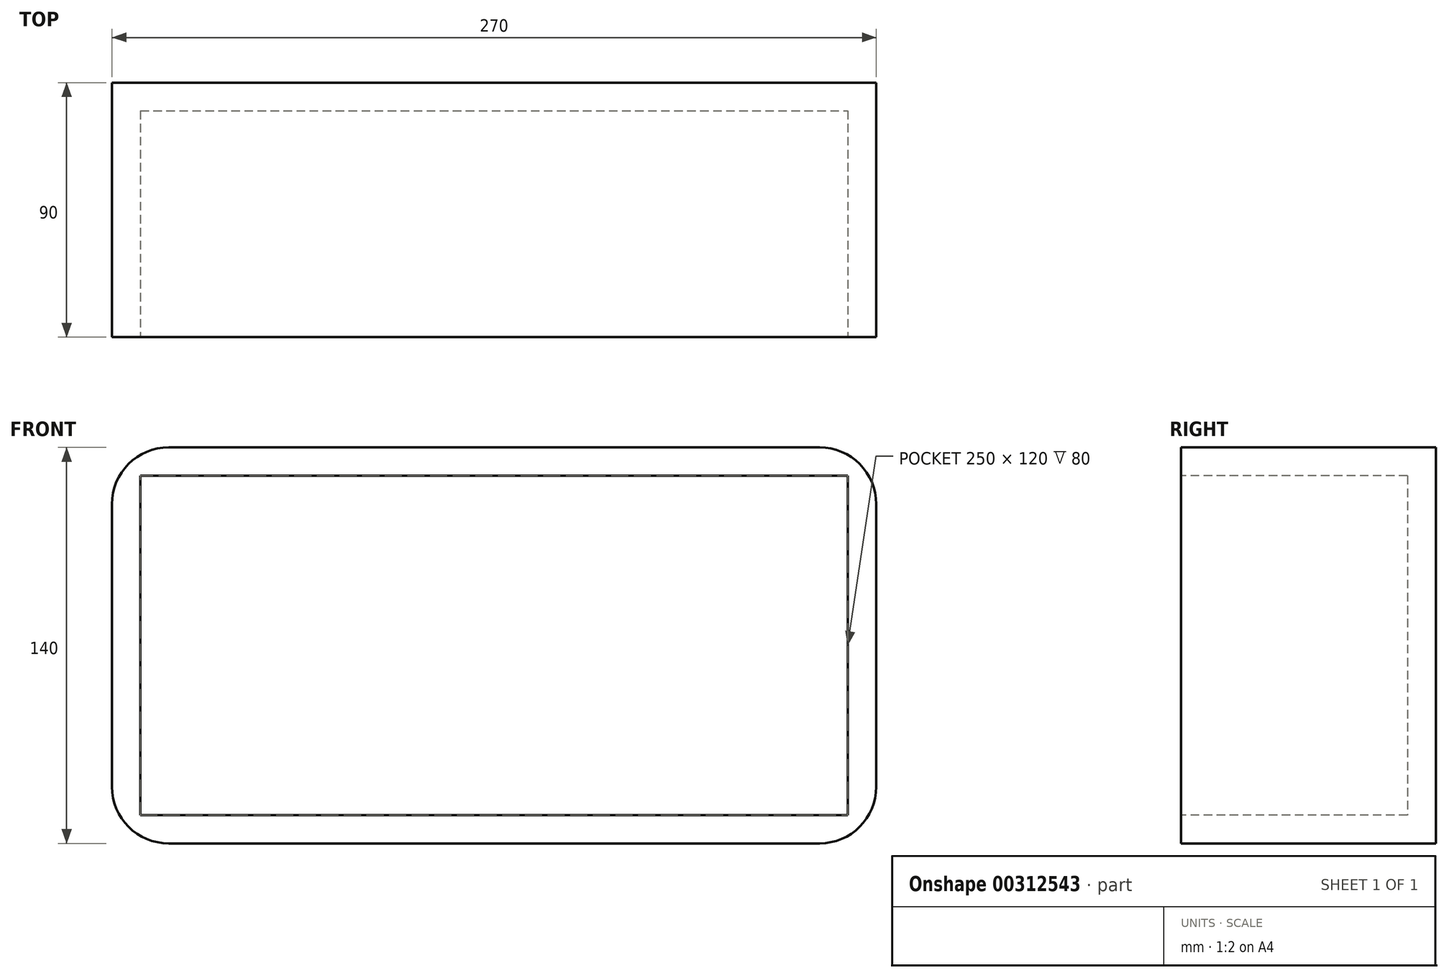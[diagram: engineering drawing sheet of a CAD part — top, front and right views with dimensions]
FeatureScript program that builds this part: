
annotation { "Feature Type Name" : "Feature", "Feature Type Description" : "" }
export const myFeature = defineFeature(function(context is Context, id is Id, definition is map)
    precondition{}
    {
        {
            var Q0;
            Q0=qCreatedBy(makeId("Front.planeOp"),FACE);
            var sketch = newSketch(context, id + "F0", { "sketchPlane" : qUnion([Q0])});
            skLineSegment(sketch, "E0.bottom", {"start": v(-135, 70) * mm, "end": v(135, 70) * mm});
            skLineSegment(sketch, "E0.top", {"start": v(-135, -70) * mm, "end": v(135, -70) * mm});
            skLineSegment(sketch, "E0.left", {"start": v(-135, 70) * mm, "end": v(-135, -70) * mm});
            skLineSegment(sketch, "E0.right", {"start": v(135, 70) * mm, "end": v(135, -70) * mm});
            skPoint(sketch, "E0.middle", {"position": v(0, 0) * mm});
            skSolve(sketch);
        }
        {
            var Q0;
            Q0=makeQuery(id+"F0.imprint","IMPRINT",FACE,{"disambiguationData":[TD([[makeQuery(id+"F0.imprint","IMPRINT",EDGE,{"derivedFrom":sQuery(id+"F0.wireOp",EDGE,"E0.bottom")}),-1.0]])]});
            extrude(context, id + "F1", {"entities" : qUnion([Q0]), "depth" : 90 * mm});
        }
        {
            var Q0;
            Q0=makeQuery(id+"F1.opExtrude","CAP_FACE",FACE,{"disambiguationData":[OSD([sQuery(id+"F0.wireOp",EDGE,"E0.bottom"),sQuery(id+"F0.wireOp",EDGE,"E0.top"),sQuery(id+"F0.wireOp",EDGE,"E0.left"),sQuery(id+"F0.wireOp",EDGE,"E0.right")])],"isStart":false});
            var sketch = newSketch(context, id + "F2", { "sketchPlane" : qUnion([Q0])});
            skLineSegment(sketch, "E1.bottom", {"start": v(-125, 60) * mm, "end": v(125, 60) * mm});
            skLineSegment(sketch, "E1.top", {"start": v(-125, -60) * mm, "end": v(125, -60) * mm});
            skLineSegment(sketch, "E1.left", {"start": v(-125, 60) * mm, "end": v(-125, -60) * mm});
            skLineSegment(sketch, "E1.right", {"start": v(125, 60) * mm, "end": v(125, -60) * mm});
            skPoint(sketch, "E1.middle", {"position": v(0, 0) * mm});
            skSolve(sketch);
        }
        {
            var Q0;
            Q0=makeQuery(id+"F2.imprint","IMPRINT",FACE,{"disambiguationData":[TD([[makeQuery(id+"F2.imprint","IMPRINT",EDGE,{"derivedFrom":sQuery(id+"F2.wireOp",EDGE,"E1.bottom")}),-1.0]])]});
            extrude(context, id + "F3", {"entities" : qUnion([Q0]), "operationType" : NewBodyOperationType.REMOVE, "oppositeDirection" : true, "depth" : 80 * mm});
        }
        {
            var Q0;
            Q0=makeQuery(id+"F1.opExtrude","SWEPT_EDGE",EDGE,{"disambiguationData":[OSD([sQuery(id+"F0.wireOp",EDGE,"E0.bottom"),sQuery(id+"F0.wireOp",EDGE,"E0.left")])]});
            var Q1;
            Q1=makeQuery(id+"F1.opExtrude","SWEPT_EDGE",EDGE,{"disambiguationData":[OSD([sQuery(id+"F0.wireOp",EDGE,"E0.bottom"),sQuery(id+"F0.wireOp",EDGE,"E0.right")])]});
            var Q2;
            Q2=makeQuery(id+"F1.opExtrude","SWEPT_EDGE",EDGE,{"disambiguationData":[OSD([sQuery(id+"F0.wireOp",EDGE,"E0.top"),sQuery(id+"F0.wireOp",EDGE,"E0.left")])]});
            var Q3;
            Q3=makeQuery(id+"F1.opExtrude","SWEPT_EDGE",EDGE,{"disambiguationData":[OSD([sQuery(id+"F0.wireOp",EDGE,"E0.top"),sQuery(id+"F0.wireOp",EDGE,"E0.right")])]});
            fillet(context, id + "F4", {"entities" : qUnion([Q0, Q1, Q2, Q3]), "radius" : 20 * mm, "tangentPropagation" : true, "allowEdgeOverflow" : false});
        }
    });
